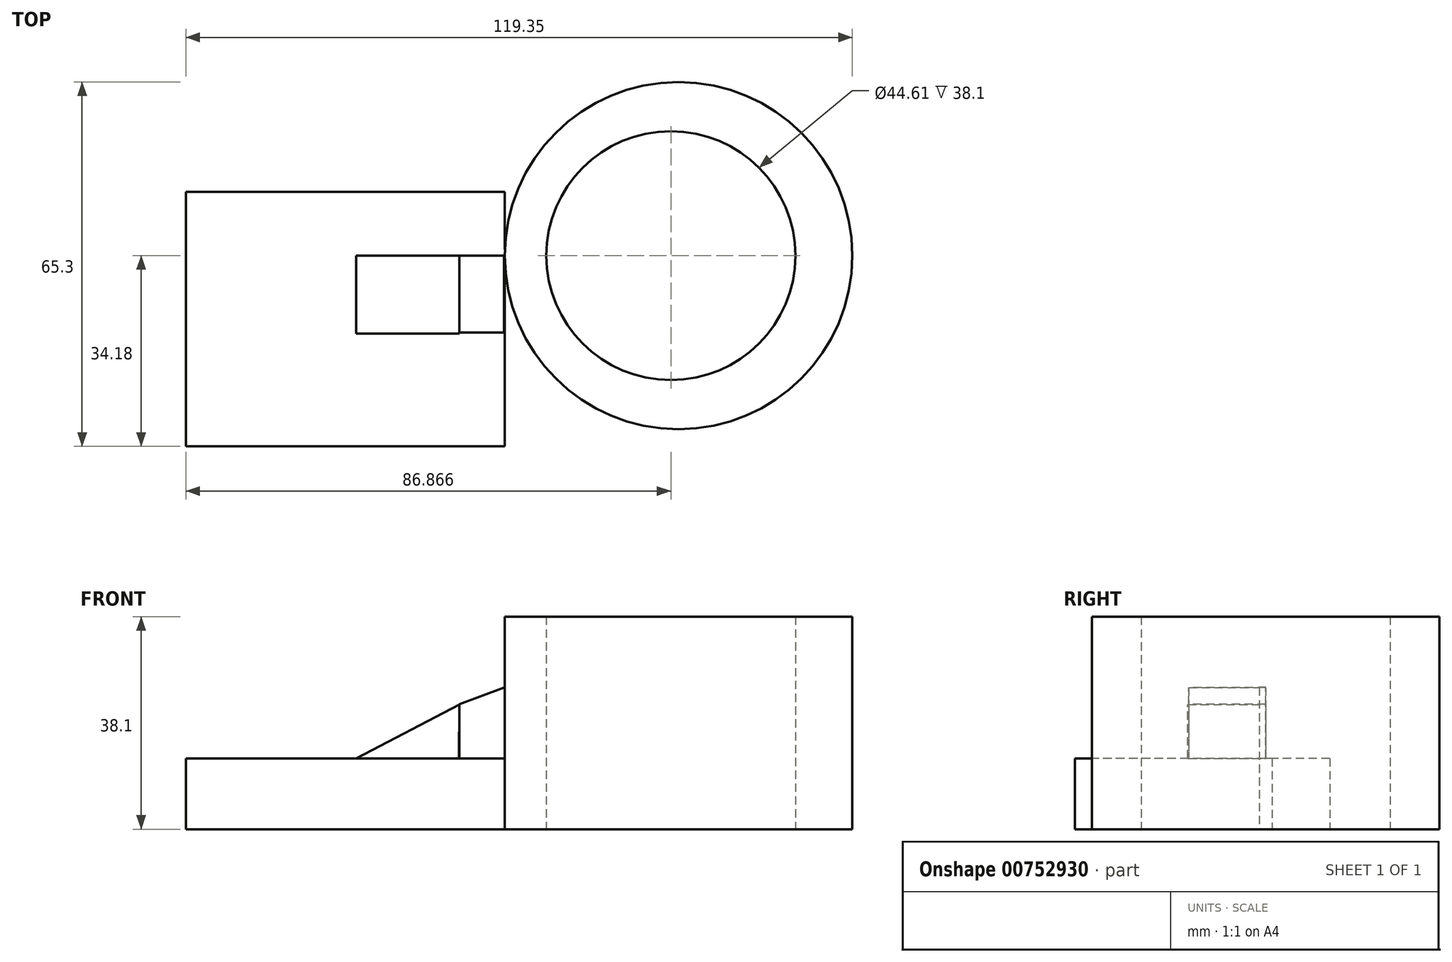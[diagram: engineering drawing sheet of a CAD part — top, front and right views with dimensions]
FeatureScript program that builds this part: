
annotation { "Feature Type Name" : "Feature", "Feature Type Description" : "" }
export const myFeature = defineFeature(function(context is Context, id is Id, definition is map)
    precondition{}
    {
        {
            var Q0;
            Q0=qCreatedBy(makeId("Top.planeOp"),FACE);
            var sketch = newSketch(context, id + "F0", { "sketchPlane" : qUnion([Q0])});
            skLineSegment(sketch, "E0.bottom", {"start": v(-57.14, 11.46) * mm, "end": v(0, 11.46) * mm});
            skLineSegment(sketch, "E0.top", {"start": v(-57.14, -34.18) * mm, "end": v(0, -34.18) * mm});
            skLineSegment(sketch, "E0.left", {"start": v(-57.14, 11.46) * mm, "end": v(-57.14, -34.18) * mm});
            skLineSegment(sketch, "E0.right", {"start": v(0, 11.46) * mm, "end": v(0, -34.18) * mm});
            skSolve(sketch);
        }
        {
            var Q0;
            Q0 = qSketchRegion(id + "F0", true);
            extrude(context, id + "F1", {"entities" : qUnion([Q0]), "depth" : 12.7 * mm, "offsetDistance" : 25.4 * mm});
        }
        {
            var Q0;
            Q0=qCreatedBy(makeId("Top.planeOp"),FACE);
            var sketch = newSketch(context, id + "F2", { "sketchPlane" : qUnion([Q0])});
            skCircle(sketch, "E1", {"center": v(31.1, 0) * mm, "radius": 31.12 * mm});
            skSolve(sketch);
        }
        {
            var Q0;
            Q0=makeQuery(id+"F2.imprint","IMPRINT",FACE,{"disambiguationData":[TD([[makeQuery(id+"F2.imprint","IMPRINT",EDGE,{"derivedFrom":sQuery(id+"F2.wireOp",EDGE,"E1")}),1.0]])]});
            extrude(context, id + "F3", {"entities" : qUnion([Q0]), "operationType" : NewBodyOperationType.ADD, "depth" : 38.1 * mm, "offsetDistance" : 25.4 * mm});
        }
        {
            var Q0;
            Q0=qCreatedBy(makeId("Top.planeOp"),FACE);
            var sketch = newSketch(context, id + "F4", { "sketchPlane" : qUnion([Q0])});
            skCircle(sketch, "E2", {"center": v(29.73, 0) * mm, "radius": 22.3 * mm});
            skSolve(sketch);
        }
        {
            var Q0;
            Q0=makeQuery(id+"F4.imprint","IMPRINT",FACE,{"disambiguationData":[TD([[makeQuery(id+"F4.imprint","IMPRINT",EDGE,{"derivedFrom":sQuery(id+"F4.wireOp",EDGE,"E2")}),1.0]])]});
            extrude(context, id + "F5", {"entities" : qUnion([Q0]), "operationType" : NewBodyOperationType.REMOVE, "depth" : 25.4 * mm, "offsetDistance" : 25.4 * mm});
        }
        {
            var Q0;
            Q0=makeQuery(id+"F5.boolean.opBoolean","COPY",FACE,{"derivedFrom":makeQuery(id+"F5.opExtrude","CAP_FACE",FACE,{"disambiguationData":[OSD([sQuery(id+"F4.wireOp",EDGE,"E2")])],"isStart":false})});
            extrude(context, id + "F6", {"entities" : qUnion([Q0]), "operationType" : NewBodyOperationType.REMOVE, "oppositeDirection" : true, "depth" : 25.4 * mm, "offsetDistance" : 25.4 * mm});
        }
        {
            var Q0;
            Q0=qCreatedBy(makeId("Top.planeOp"),FACE);
            var sketch = newSketch(context, id + "F7", { "sketchPlane" : qUnion([Q0])});
            skLineSegment(sketch, "E3", {"start": v(-33.54, 0) * mm, "end": v(-33.54, -13.76) * mm});
            skLineSegment(sketch, "E4", {"start": v(-33.54, -13.76) * mm, "end": v(0, -13.76) * mm});
            skLineSegment(sketch, "E5", {"start": v(0, -13.76) * mm, "end": v(0, 0) * mm});
            skLineSegment(sketch, "E6", {"start": v(0, 0) * mm, "end": v(-33.54, 0) * mm});
            skSolve(sketch);
        }
        {
            var Q0;
            Q0=makeQuery(id+"F7.imprint","IMPRINT",FACE,{"disambiguationData":[TD([[makeQuery(id+"F7.imprint","IMPRINT",EDGE,{"derivedFrom":sQuery(id+"F7.wireOp",EDGE,"E3")}),1.0]])]});
            extrude(context, id + "F8", {"entities" : qUnion([Q0]), "operationType" : NewBodyOperationType.ADD, "depth" : 25.4 * mm, "offsetDistance" : 25.4 * mm});
        }
        {
            var Q0;
            Q0=qCreatedBy(makeId("Front.planeOp"),FACE);
            var sketch = newSketch(context, id + "F9", { "sketchPlane" : qUnion([Q0])});
            skLineSegment(sketch, "E7", {"start": v(-33.48, 12.78) * mm, "end": v(0, 25.47) * mm});
            skLineSegment(sketch, "E8", {"start": v(0, 25.47) * mm, "end": v(-33.48, 25.47) * mm});
            skLineSegment(sketch, "E9", {"start": v(-33.48, 25.47) * mm, "end": v(-33.48, 12.78) * mm});
            skSolve(sketch);
        }
        {
            var Q0;
            Q0 = qSketchRegion(id + "F9", true);
            extrude(context, id + "F10", {"entities" : qUnion([Q0]), "operationType" : NewBodyOperationType.ADD, "depth" : 101.6 * mm, "offsetDistance" : 25.4 * mm});
        }
        {
            var Q0;
            Q0=makeQuery(id+"F10.opExtrude","CAP_FACE",FACE,{"disambiguationData":[OSD([sQuery(id+"F9.wireOp",EDGE,"E7"),sQuery(id+"F9.wireOp",EDGE,"E8"),sQuery(id+"F9.wireOp",EDGE,"E9")])],"isStart":false});
            extrude(context, id + "F11", {"entities" : qUnion([Q0]), "operationType" : NewBodyOperationType.REMOVE, "oppositeDirection" : true, "depth" : 25.4 * mm, "offsetDistance" : 25.4 * mm});
        }
        {
            var Q0;
            Q0=makeQuery(id+"F11.boolean.opBoolean","COPY",FACE,{"derivedFrom":makeQuery(id+"F11.opExtrude","CAP_FACE",FACE,{"disambiguationData":[OSD([sQuery(id+"F9.wireOp",EDGE,"E7"),sQuery(id+"F9.wireOp",EDGE,"E8"),sQuery(id+"F9.wireOp",EDGE,"E9")])],"isStart":false})});
            extrude(context, id + "F12", {"entities" : qUnion([Q0]), "operationType" : NewBodyOperationType.REMOVE, "oppositeDirection" : true, "depth" : 25.4 * mm, "offsetDistance" : 25.4 * mm});
        }
        {
            var Q0;
            Q0=makeQuery(id+"F12.boolean.opBoolean","COPY",FACE,{"derivedFrom":makeQuery(id+"F12.opExtrude","CAP_FACE",FACE,{"disambiguationData":[OSD([sQuery(id+"F9.wireOp",EDGE,"E7"),sQuery(id+"F9.wireOp",EDGE,"E8"),sQuery(id+"F9.wireOp",EDGE,"E9")])],"isStart":false})});
            extrude(context, id + "F13", {"entities" : qUnion([Q0]), "operationType" : NewBodyOperationType.REMOVE, "oppositeDirection" : true, "depth" : 25.4 * mm, "offsetDistance" : 25.4 * mm});
        }
        {
            var Q0;
            Q0=makeQuery(id+"F13.boolean.opBoolean","COPY",FACE,{"derivedFrom":makeQuery(id+"F13.opExtrude","CAP_FACE",FACE,{"disambiguationData":[OSD([sQuery(id+"F9.wireOp",EDGE,"E7"),sQuery(id+"F9.wireOp",EDGE,"E8"),sQuery(id+"F9.wireOp",EDGE,"E9")])],"isStart":false})});
            extrude(context, id + "F14", {"entities" : qUnion([Q0]), "operationType" : NewBodyOperationType.REMOVE, "oppositeDirection" : true, "depth" : 25.4 * mm, "offsetDistance" : 25.4 * mm});
        }
        {
            var Q0;
            Q0=makeQuery(id+"F8.opExtrude","SWEPT_FACE",FACE,{"disambiguationData":[OSD([sQuery(id+"F7.wireOp",EDGE,"E3")])]});
            extrude(context, id + "F15", {"entities" : qUnion([Q0]), "operationType" : NewBodyOperationType.REMOVE, "oppositeDirection" : true, "depth" : 25.4 * mm, "offsetDistance" : 25.4 * mm});
        }
        {
            var Q0;
            Q0=qCreatedBy(makeId("Front.planeOp"),FACE);
            var sketch = newSketch(context, id + "F16", { "sketchPlane" : qUnion([Q0])});
            skLineSegment(sketch, "E10", {"start": v(-8.16, 22.3) * mm, "end": v(-26.66, 12.7) * mm});
            skLineSegment(sketch, "E11", {"start": v(-26.66, 12.7) * mm, "end": v(-8.21, 12.7) * mm});
            skLineSegment(sketch, "E12", {"start": v(-8.21, 12.7) * mm, "end": v(-8.16, 22.3) * mm});
            skSolve(sketch);
        }
        {
            var Q0;
            Q0=makeQuery(id+"F16.imprint","IMPRINT",FACE,{"disambiguationData":[TD([[makeQuery(id+"F16.imprint","IMPRINT",EDGE,{"derivedFrom":sQuery(id+"F16.wireOp",EDGE,"E10")}),1.0]])]});
            extrude(context, id + "F17", {"entities" : qUnion([Q0]), "depth" : 13.97 * mm, "offsetDistance" : 25.4 * mm});
        }
    });
